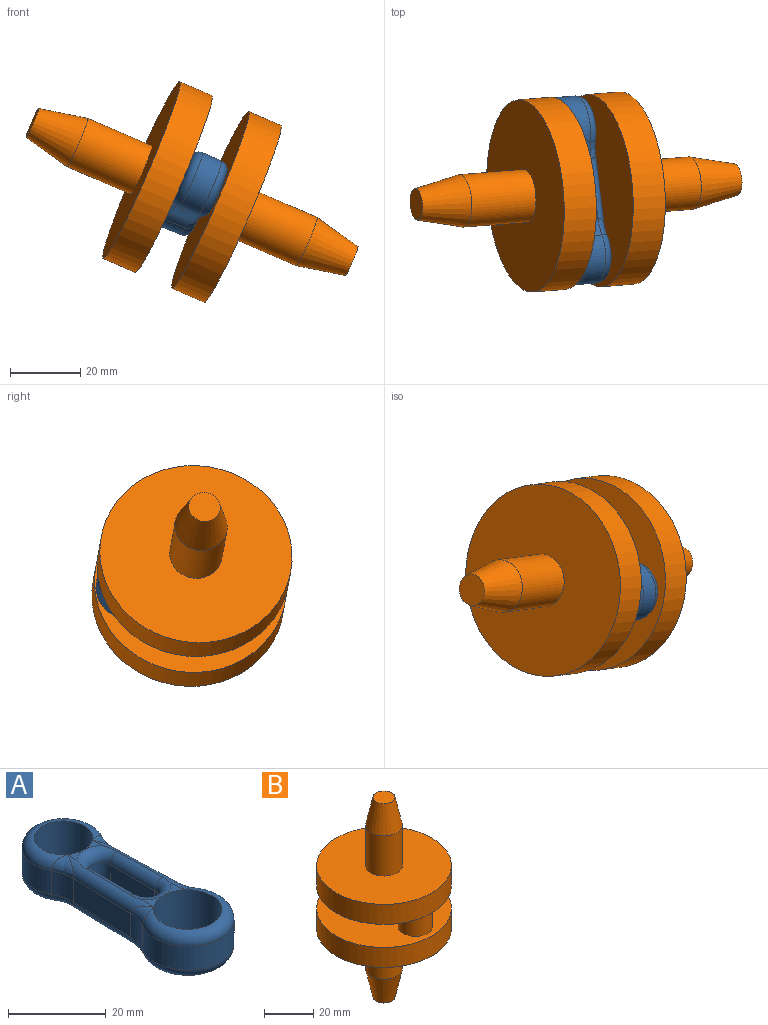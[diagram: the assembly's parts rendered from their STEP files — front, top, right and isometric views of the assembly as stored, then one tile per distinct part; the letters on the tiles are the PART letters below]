
ASSEMBLY  parts=2 mates=1
PART A: 46 faces, bbox 20.6x55.5x11 mm
  f0: plane 3.71x2.87mm, normal (0,0,1), area 3.3mm2, adj f13,f29,f32
  f1: plane 3.71x2.87mm, normal (0,0,1), area 3.3mm2, adj f13,f29,f31
  f2: plane 4.35x3.86mm, normal (0,0,1), area 5.1mm2, adj f15,f27,f32
  f3: plane 4.35x3.86mm, normal (0,0,-1), area 5.1mm2, adj f15,f20,f24
  f4: plane 4.35x3.86mm, normal (0,0,-1), area 5.1mm2, adj f15,f23,f24
  f5: plane 3.71x2.87mm, normal (0,0,-1), area 3.3mm2, adj f13,f20,f22
  f6: cylinder r=8.5mm len=17mm, axis (0,0,-1), area 211.1mm2, adj f18,f30,f35,f38
  f7: plane 17.13x6mm, normal (-1,0.03,0), area 102.8mm2, adj f23,f31,f35,f41
  f8: cylinder r=9.5mm len=19mm, axis (0,0,-1), area 240.6mm2, adj f19,f33,f41,f44
  f9: cylinder r=2.5mm len=6mm, axis (0,0,-1), area 47.1mm2, adj f10,f14,f22,f29
  f10: plane 13x6mm, normal (-1,0,0), area 78mm2, adj f9,f11,f21,f28
  f11: cylinder r=2.5mm len=6mm, axis (0,0,-1), area 47.1mm2, adj f10,f14,f24,f27
  f12: plane 17.13x6mm, normal (1,0.03,0), area 102.8mm2, adj f20,f32,f38,f44
  f13: cylinder r=6mm len=12mm, axis (0,0,-1), area 414.7mm2, adj f0,f1,f5,f17,f18,f30
  f14: plane 13x6mm, normal (1,0,0), area 78mm2, adj f9,f11,f25,f26
  f15: cylinder r=7mm len=14mm, axis (0,0,-1), area 483.8mm2, adj f2,f3,f4,f16,f19,f33
  f16: plane 4.35x3.86mm, normal (0,0,1), area 5.1mm2, adj f15,f27,f31
  f17: plane 3.71x2.87mm, normal (0,0,-1), area 3.3mm2, adj f13,f22,f23
  f18: torus R=6mm, axis (0,0,1), area 129mm2, adj f6,f13,f34,f37
  f19: torus R=7mm, axis (0,0,1), area 148.2mm2, adj f8,f15,f40,f43
  f20: cylinder r=2.5mm len=25.81mm, axis (-0.03,1,0), area 69.7mm2, adj f3,f5,f12,f21,f22,f24,f37,f43
  f21: cylinder r=2.5mm len=13mm, axis (0,-1,0), area 44.4mm2, adj f10,f20,f22,f24
  f22: torus R=5mm, axis (0,0,1), area 39.1mm2, adj f5,f9,f17,f20,f21,f23,f25
  f23: cylinder r=2.5mm len=25.81mm, axis (-0.03,-1,0), area 69.7mm2, adj f4,f7,f17,f22,f24,f25,f34,f40
  f24: torus R=5mm, axis (0,0,1), area 40.9mm2, adj f3,f4,f11,f20,f21,f23,f25
  f25: cylinder r=2.5mm len=13mm, axis (0,1,0), area 44.4mm2, adj f14,f22,f23,f24
  f26: cylinder r=2.5mm len=13mm, axis (0,-1,0), area 44.4mm2, adj f14,f27,f29,f31
  f27: torus R=5mm, axis (0,0,1), area 40.9mm2, adj f2,f11,f16,f26,f28,f31,f32
  f28: cylinder r=2.5mm len=13mm, axis (0,1,0), area 44.4mm2, adj f10,f27,f29,f32
  f29: torus R=5mm, axis (0,0,1), area 39.1mm2, adj f0,f1,f9,f26,f28,f31,f32
  f30: torus R=6mm, axis (0,0,1), area 129mm2, adj f6,f13,f36,f39
  f31: cylinder r=2.5mm len=25.81mm, axis (0.03,1,0), area 69.7mm2, adj f1,f7,f16,f26,f27,f29,f36,f42
  f32: cylinder r=2.5mm len=25.81mm, axis (0.03,-1,0), area 69.7mm2, adj f0,f2,f12,f27,f28,f29,f39,f45
  f33: torus R=7mm, axis (0,0,1), area 148.2mm2, adj f8,f15,f42,f45
  f34: bspline ~5.06x3.84mm, area 15.5mm2, adj f18,f23,f35
  f35: cylinder r=10mm len=6mm, axis (0,0,-1), area 31.6mm2, adj f6,f7,f34,f36
  f36: bspline ~5.06x3.84mm, area 15.5mm2, adj f30,f31,f35
  f37: bspline ~5.06x3.84mm, area 15.5mm2, adj f18,f20,f38
  f38: cylinder r=10mm len=6mm, axis (0,0,-1), area 31.6mm2, adj f6,f12,f37,f39
  f39: bspline ~5.06x3.84mm, area 15.5mm2, adj f30,f32,f38
  f40: bspline ~4.87x3.81mm, area 14.9mm2, adj f19,f23,f41
  f41: cylinder r=10mm len=6mm, axis (0,0,-1), area 30.7mm2, adj f7,f8,f40,f42
  f42: bspline ~4.87x3.81mm, area 14.9mm2, adj f31,f33,f41
  f43: bspline ~4.87x3.81mm, area 14.9mm2, adj f19,f20,f44
  f44: cylinder r=10mm len=6mm, axis (0,0,-1), area 30.7mm2, adj f8,f12,f43,f45
  f45: bspline ~4.87x3.81mm, area 14.9mm2, adj f32,f33,f44
PART B: 13 faces, bbox 55x55x99.5 mm
  f0: cylinder r=7.5mm len=20mm, axis (0,0,-1), area 942.5mm2, adj f4,f5
  f1: plane 9x9mm, normal (0,0,1), area 63.6mm2, adj f5
  f2: cylinder r=27.5mm len=55mm, axis (0,0,1), area 1727.9mm2, adj f3,f4
  f3: plane 55x55mm, normal (0,0,-1), area 2221.9mm2, adj f2,f6
  f4: plane 55x55mm, normal (0,0,1), area 2199.1mm2, adj f0,f2
  f5: cone r=4.5mm half-angle=12.1deg, axis (0,0,-1), area 539.8mm2, adj f0,f1
  f6: cylinder r=7mm len=14mm, axis (0,0,1), area 505.8mm2, adj f3,f9
  f7: cylinder r=27.5mm len=55mm, axis (0,0,1), area 1727.9mm2, adj f8,f9
  f8: plane 55x55mm, normal (0,0,-1), area 2199.1mm2, adj f7,f10
  f9: plane 55x55mm, normal (0,0,1), area 2221.9mm2, adj f6,f7
  f10: cylinder r=7.5mm len=20mm, axis (0,0,1), area 942.5mm2, adj f8,f12
  f11: plane 9x9mm, normal (0,0,-1), area 63.6mm2, adj f12
  f12: cone r=4.5mm half-angle=12.1deg, axis (0,0,1), area 539.8mm2, adj f10,f11
PLACE A rot(axis=(0.55,-0.02,-0.83),169.8deg) t=(-116.78,14.92,-58.76)mm
PLACE B rot(axis=(0.55,-0.02,-0.83),169.8deg) t=(-178.85,41.75,-143.72)mm
MATE revolute B.f6 <-> A.f8  axis (-0.92,-0.07,0.4) through (-121.82,14.53,-56.58)mm
